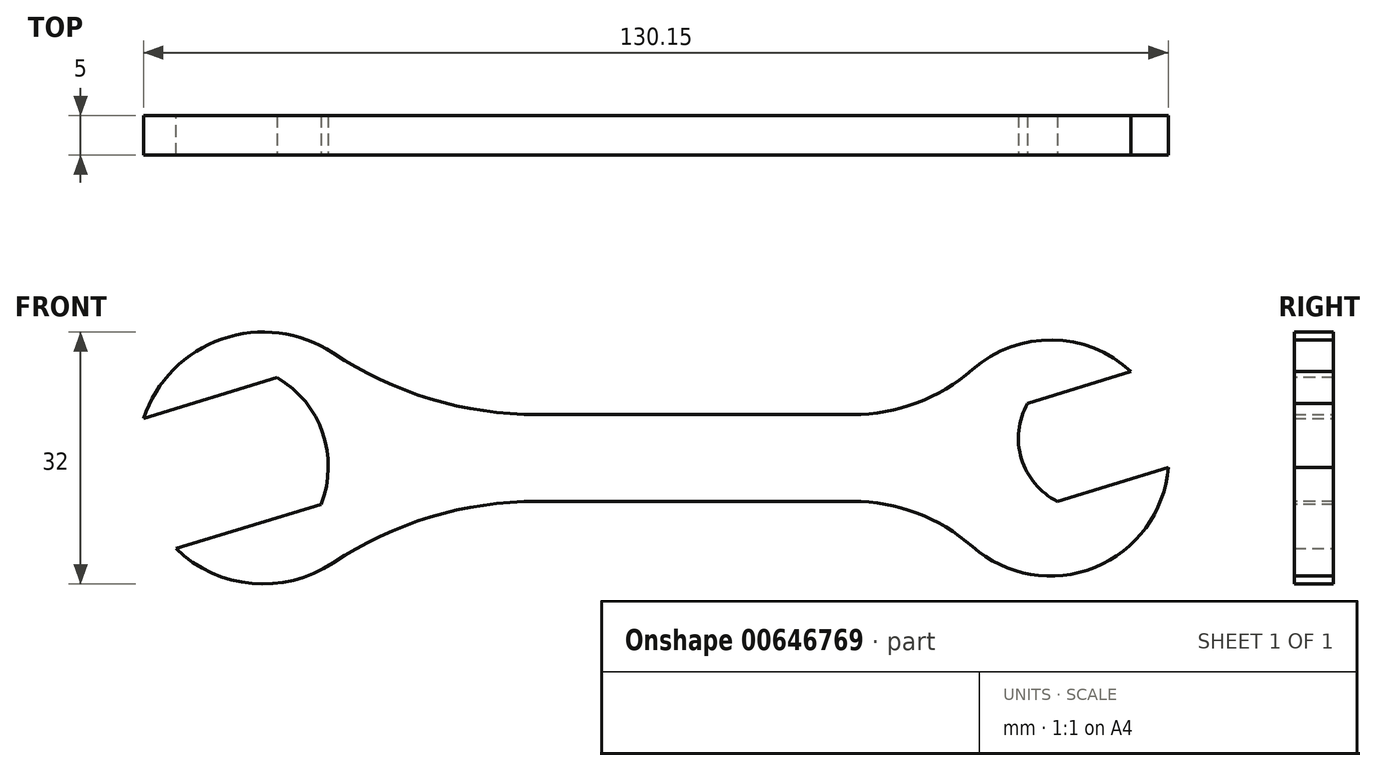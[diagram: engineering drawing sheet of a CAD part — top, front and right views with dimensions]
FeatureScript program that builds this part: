
annotation { "Feature Type Name" : "Feature", "Feature Type Description" : "" }
export const myFeature = defineFeature(function(context is Context, id is Id, definition is map)
    precondition{}
    {
        {
            var Q0;
            Q0=qCreatedBy(makeId("Front.planeOp"),FACE);
            var sketch = newSketch(context, id + "F0", { "sketchPlane" : qUnion([Q0])});
            skLineSegment(sketch, "E0.bottom", {"start": v(-50, 5.5) * mm, "end": v(50, 5.5) * mm});
            skLineSegment(sketch, "E0.top", {"start": v(-50, -5.5) * mm, "end": v(50, -5.5) * mm});
            skLineSegment(sketch, "E0.left", {"start": v(-50, 5.5) * mm, "end": v(-50, -5.5) * mm});
            skLineSegment(sketch, "E0.right", {"start": v(50, 5.5) * mm, "end": v(50, -5.5) * mm});
            skPoint(sketch, "E0.middle", {"position": v(0, 0) * mm});
            skCircle(sketch, "E1", {"center": v(50, 0) * mm, "radius": 15 * mm});
            skCircle(sketch, "E2", {"center": v(-50, 0) * mm, "radius": 16 * mm});
            skSolve(sketch);
        }
        {
            var Q0;
            Q0 = qSketchRegion(id + "F0", true);
            extrude(context, id + "F1", {"entities" : qUnion([Q0]), "depth" : 5 * mm, "offsetDistance" : 25 * mm});
        }
        {
            var Q0;
            Q0=makeQuery(id+"F1.opExtrude","CAP_FACE",FACE,{"disambiguationData":[OSD([sQuery(id+"F0.wireOp",EDGE,"E0.bottom"),sQuery(id+"F0.wireOp",EDGE,"E0.top"),sQuery(id+"F0.wireOp",EDGE,"E1"),sQuery(id+"F0.wireOp",EDGE,"E2")])],"isStart":false});
            var sketch = newSketch(context, id + "F2", { "sketchPlane" : qUnion([Q0])});
            skPoint(sketch, "E3", {"position": v(-50, 0) * mm});
            skArc(sketch, "E4", {"start": v(-42.67, -5.88) * mm, "mid": v(-42.45, 3.2) * mm, "end": v(-48.22, 10.2) * mm});
            skLineSegment(sketch, "E5", {"start": v(-42.67, -5.88) * mm, "end": v(-95.84, -22.14) * mm});
            skLineSegment(sketch, "E6", {"start": v(-95.84, -22.14) * mm, "end": v(-100.81, -5.88) * mm});
            skLineSegment(sketch, "E7", {"start": v(-100.81, -5.88) * mm, "end": v(-48.22, 10.2) * mm});
            skLineSegment(sketch, "E8", {"start": v(-35.24, -12.94) * mm, "end": v(-68.9, -12.94) * mm, "construction": true});
            skSolve(sketch);
        }
        {
            var Q0;
            Q0 = qSketchRegion(id + "F2", true);
            extrude(context, id + "F3", {"entities" : qUnion([Q0]), "operationType" : NewBodyOperationType.REMOVE, "oppositeDirection" : true, "depth" : 25 * mm, "offsetDistance" : 25 * mm});
        }
        {
            var Q0;
            Q0=makeQuery(id+"F1.opExtrude","SWEPT_EDGE",EDGE,{"disambiguationData":[OSD([sQuery(id+"F0.wireOp",EDGE,"E0.bottom"),sQuery(id+"F0.wireOp",EDGE,"E2")])]});
            var Q1;
            Q1=makeQuery(id+"F1.opExtrude","SWEPT_EDGE",EDGE,{"disambiguationData":[OSD([sQuery(id+"F0.wireOp",EDGE,"E0.top"),sQuery(id+"F0.wireOp",EDGE,"E2")])]});
            fillet(context, id + "F4", {"entities" : qUnion([Q0, Q1]), "radius" : 47 * mm, "tangentPropagation" : true, "allowEdgeOverflow" : false});
        }
        {
            var Q0;
            Q0=makeQuery(id+"F1.opExtrude","SWEPT_EDGE",EDGE,{"disambiguationData":[OSD([sQuery(id+"F0.wireOp",EDGE,"E0.top"),sQuery(id+"F0.wireOp",EDGE,"E1")])]});
            var Q1;
            Q1=makeQuery(id+"F1.opExtrude","SWEPT_EDGE",EDGE,{"disambiguationData":[OSD([sQuery(id+"F0.wireOp",EDGE,"E0.bottom"),sQuery(id+"F0.wireOp",EDGE,"E1")])]});
            fillet(context, id + "F5", {"entities" : qUnion([Q0, Q1]), "radius" : 23 * mm, "tangentPropagation" : true, "allowEdgeOverflow" : false});
        }
        {
            var Q0;
            Q0=makeQuery(id+"F1.opExtrude","CAP_FACE",FACE,{"disambiguationData":[OSD([sQuery(id+"F0.wireOp",EDGE,"E0.bottom"),sQuery(id+"F0.wireOp",EDGE,"E0.top"),sQuery(id+"F0.wireOp",EDGE,"E1"),sQuery(id+"F0.wireOp",EDGE,"E2")])],"isStart":false});
            var sketch = newSketch(context, id + "F6", { "sketchPlane" : qUnion([Q0])});
            skPoint(sketch, "E9", {"position": v(50, 0) * mm});
            skArc(sketch, "E10", {"start": v(47.06, 6.93) * mm, "mid": v(46.3, -0.1) * mm, "end": v(50.86, -5.5) * mm});
            skLineSegment(sketch, "E11", {"start": v(47.06, 6.93) * mm, "end": v(72.88, 14.83) * mm});
            skLineSegment(sketch, "E12", {"start": v(72.88, 14.83) * mm, "end": v(76.68, 2.4) * mm});
            skLineSegment(sketch, "E13", {"start": v(76.68, 2.4) * mm, "end": v(50.86, -5.5) * mm});
            skLineSegment(sketch, "E14", {"start": v(11.64, -5.5) * mm, "end": v(96.3, -5.5) * mm, "construction": true});
            skLineSegment(sketch, "E15", {"start": v(76.68, 2.4) * mm, "end": v(46.55, -6.82) * mm, "construction": true});
            skSolve(sketch);
        }
        {
            var Q0;
            Q0 = qSketchRegion(id + "F6", true);
            extrude(context, id + "F7", {"entities" : qUnion([Q0]), "operationType" : NewBodyOperationType.REMOVE, "oppositeDirection" : true, "depth" : 25 * mm, "offsetDistance" : 25 * mm});
        }
    });
